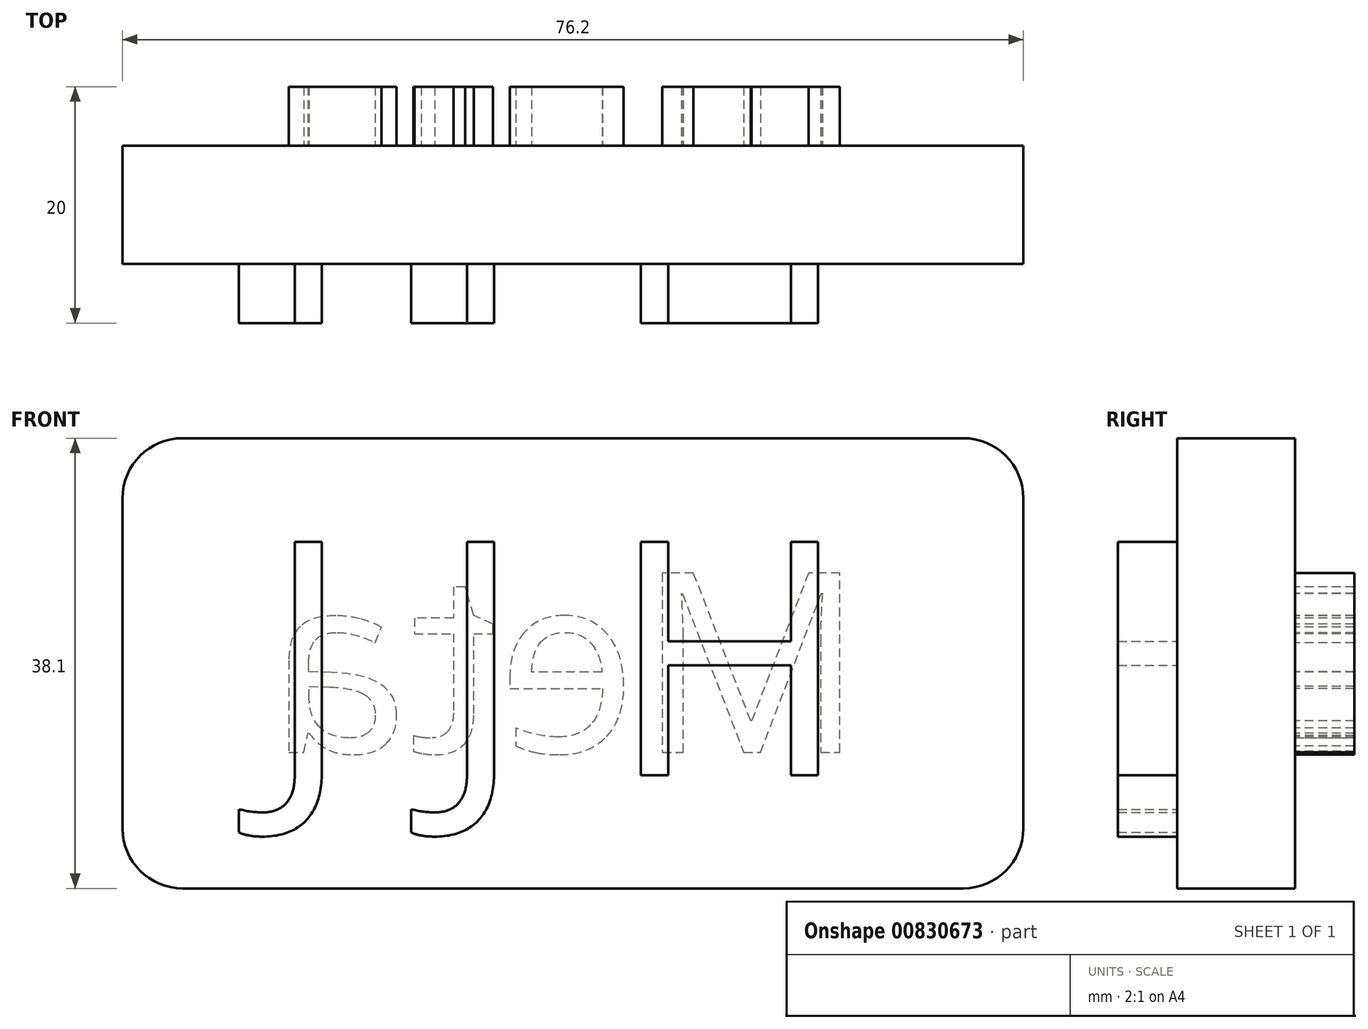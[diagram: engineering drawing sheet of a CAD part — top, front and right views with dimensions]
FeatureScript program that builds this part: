
annotation { "Feature Type Name" : "Feature", "Feature Type Description" : "" }
export const myFeature = defineFeature(function(context is Context, id is Id, definition is map)
    precondition{}
    {
        {
            var Q0;
            Q0=qCreatedBy(makeId("Front.planeOp"),FACE);
            var sketch = newSketch(context, id + "F0", { "sketchPlane" : qUnion([Q0])});
            skLineSegment(sketch, "E0.bottom", {"start": v(0, 0) * mm, "end": v(76.2, 0) * mm});
            skLineSegment(sketch, "E0.top", {"start": v(0, 38.1) * mm, "end": v(76.2, 38.1) * mm});
            skLineSegment(sketch, "E0.left", {"start": v(0, 0) * mm, "end": v(0, 38.1) * mm});
            skLineSegment(sketch, "E0.right", {"start": v(76.2, 0) * mm, "end": v(76.2, 38.1) * mm});
            skSolve(sketch);
        }
        {
            var Q0;
            Q0 = qSketchRegion(id + "F0", true);
            extrude(context, id + "F1", {"entities" : qUnion([Q0]), "depth" : 10 * mm, "offsetDistance" : 25.4 * mm});
        }
        {
            var Q0;
            Q0=makeQuery(id+"F1.opExtrude","CAP_FACE",FACE,{"disambiguationData":[OSD([sQuery(id+"F0.wireOp",EDGE,"E0.bottom"),sQuery(id+"F0.wireOp",EDGE,"E0.top"),sQuery(id+"F0.wireOp",EDGE,"E0.left"),sQuery(id+"F0.wireOp",EDGE,"E0.right")])],"isStart":false});
            var sketch = newSketch(context, id + "F2", { "sketchPlane" : qUnion([Q0])});
            skText(sketch, "E1", { "text": "J J H", "fontName": "OpenSans-Regular.ttf"});
            const initialGuessF2  = {"E1": [0.012, 0.00958, 1, 0, 0.01991]};
            skSetInitialGuess(sketch, initialGuessF2);
            skSolve(sketch);
        }
        {
            var Q0;
            Q0 = qSketchRegion(id + "F2", true);
            extrude(context, id + "F3", {"entities" : qUnion([Q0]), "operationType" : NewBodyOperationType.ADD, "depth" : 5 * mm, "offsetDistance" : 25.4 * mm});
        }
        {
            var Q0;
            Q0=makeQuery(id+"F1.opExtrude","CAP_FACE",FACE,{"disambiguationData":[OSD([sQuery(id+"F0.wireOp",EDGE,"E0.bottom"),sQuery(id+"F0.wireOp",EDGE,"E0.top"),sQuery(id+"F0.wireOp",EDGE,"E0.left"),sQuery(id+"F0.wireOp",EDGE,"E0.right")])],"isStart":true});
            var sketch = newSketch(context, id + "F4", { "sketchPlane" : qUnion([Q0])});
            skText(sketch, "E2", { "text": "Meta", "fontName": "OpenSans-Regular.ttf"});
            const initialGuessF4  = {"E2": [-0.06277, 0.01152, 1, 0, 0.0153]};
            skSetInitialGuess(sketch, initialGuessF4);
            skSolve(sketch);
        }
        {
            var Q0;
            Q0 = qSketchRegion(id + "F4", true);
            extrude(context, id + "F5", {"entities" : qUnion([Q0]), "operationType" : NewBodyOperationType.ADD, "depth" : 5 * mm, "offsetDistance" : 25.4 * mm});
        }
        {
            var Q0;
            Q0=makeQuery(id+"F1.opExtrude","SWEPT_EDGE",EDGE,{"disambiguationData":[OSD([sQuery(id+"F0.wireOp",EDGE,"E0.top"),sQuery(id+"F0.wireOp",EDGE,"E0.left")])]});
            var Q1;
            Q1=makeQuery(id+"F1.opExtrude","SWEPT_EDGE",EDGE,{"disambiguationData":[OSD([sQuery(id+"F0.wireOp",EDGE,"E0.bottom"),sQuery(id+"F0.wireOp",EDGE,"E0.left")])]});
            var Q2;
            Q2=makeQuery(id+"F1.opExtrude","SWEPT_EDGE",EDGE,{"disambiguationData":[OSD([sQuery(id+"F0.wireOp",EDGE,"E0.bottom"),sQuery(id+"F0.wireOp",EDGE,"E0.right")])]});
            var Q3;
            Q3=makeQuery(id+"F1.opExtrude","SWEPT_EDGE",EDGE,{"disambiguationData":[OSD([sQuery(id+"F0.wireOp",EDGE,"E0.top"),sQuery(id+"F0.wireOp",EDGE,"E0.right")])]});
            fillet(context, id + "F6", {"entities" : qUnion([Q0, Q1, Q2, Q3]), "radius" : 5.08 * mm, "tangentPropagation" : true, "allowEdgeOverflow" : false});
        }
    });
